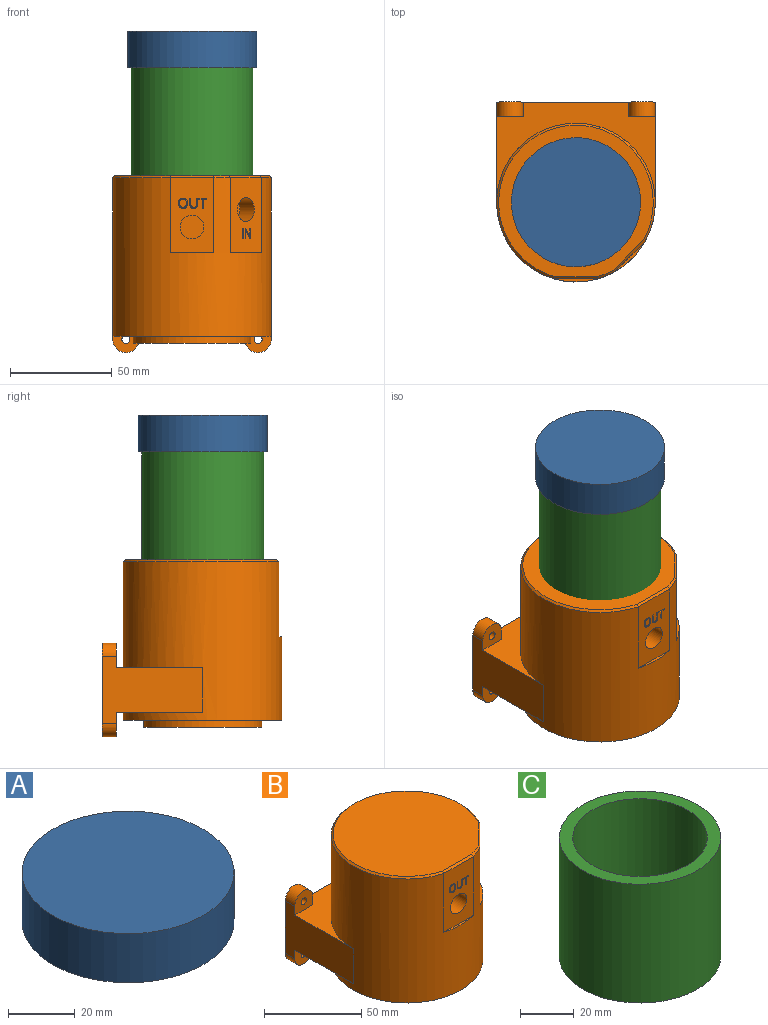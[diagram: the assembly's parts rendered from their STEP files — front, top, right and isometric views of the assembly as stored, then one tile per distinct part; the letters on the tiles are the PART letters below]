
ASSEMBLY  parts=3 mates=2
PART A: 3 faces, bbox 63.5x63.5x18 mm
  f0: cylinder r=31.75mm len=63.5mm, axis (0,0,-1), area 3590.8mm2, adj f1,f2
  f1: plane 63.5x63.5mm, normal (0,0,1), area 3166.9mm2, adj f0
  f2: plane 63.5x63.5mm, normal (0,0,-1), area 3166.9mm2, adj f0
PART B: 101 faces, bbox 78x88.5x87 mm
  f0: plane 37x15.15mm, normal (0.71,-0.71,0), area 674.2mm2, adj f5,f29,f32,f76,f77,f78,f79,f81
  f1: plane 37x21.42mm, normal (0,-1,0), area 655.2mm2, adj f5,f28,f30,f34,f35,f36,f37,f38
  f2: plane 76x74.5mm, normal (0,0,1), area 4494mm2, adj f97,f98,f99,f100
  f3: plane 78x49.5mm, normal (0,0,1), area 1289.8mm2, adj f5,f6,f7,f8,f9,f12,f19,f20
  f4: plane 78x49.5mm, normal (0,0,-1), area 1289.8mm2, adj f5,f6,f7,f8,f15,f16,f21,f24
  f5: cylinder r=39mm len=78mm, axis (0,0,-1), area 14811.9mm2, adj f0,f1,f3,f4,f6,f8,f25,f28
  f6: plane 49.5x33mm, normal (-1,0,0), area 1166mm2, adj f3,f4,f5,f7,f17,f20,f22,f24
  f7: plane 78x46mm, normal (0,1,0), area 2217.2mm2, adj f3,f4,f6,f8,f9,f10,f11,f13
  f8: plane 49.5x33mm, normal (1,0,0), area 1166mm2, adj f3,f4,f5,f7,f10,f12,f13,f16
  f9: plane 7x5.5mm, normal (-1,0,0), area 38.5mm2, adj f3,f7,f10,f12
  f10: cylinder r=6.5mm len=13mm, axis (0,1,0), area 142.9mm2, adj f7,f8,f9,f12
  f11: cylinder r=2mm len=7mm, axis (0,1,0), area 88mm2, adj f7,f12
  f12: plane 13x12mm, normal (0,-1,0), area 125.3mm2, adj f3,f8,f9,f10,f11
  f13: cylinder r=6.5mm len=13mm, axis (0,1,0), area 142.9mm2, adj f7,f8,f15,f16
  f14: cylinder r=2mm len=7mm, axis (0,1,0), area 88mm2, adj f7,f16
  f15: plane 7x5.5mm, normal (-1,0,0), area 38.5mm2, adj f4,f7,f13,f16
  f16: plane 13x12mm, normal (0,-1,0), area 125.3mm2, adj f4,f8,f13,f14,f15
  f17: cylinder r=6.5mm len=13mm, axis (0,1,0), area 142.9mm2, adj f6,f7,f19,f20
  f18: cylinder r=2mm len=7mm, axis (0,1,0), area 88mm2, adj f7,f20
  f19: plane 7x5.5mm, normal (1,0,0), area 38.5mm2, adj f3,f7,f17,f20
  f20: plane 13x12mm, normal (0,-1,0), area 125.3mm2, adj f3,f6,f17,f18,f19
  f21: plane 7x5.5mm, normal (1,0,0), area 38.5mm2, adj f4,f7,f22,f24
  f22: cylinder r=6.5mm len=13mm, axis (0,1,0), area 142.9mm2, adj f6,f7,f21,f24
  f23: cylinder r=2mm len=7mm, axis (0,1,0), area 88mm2, adj f7,f24
  f24: plane 13x12mm, normal (0,-1,0), area 125.3mm2, adj f4,f6,f21,f22,f23
  f25: plane 78x78mm, normal (0,0,-1), area 2136.3mm2, adj f5,f26
  f26: cylinder r=29mm len=58mm, axis (0,0,1), area 637.7mm2, adj f25,f27
  f27: plane 58x58mm, normal (0,0,-1), area 2642.1mm2, adj f26
  f28: plane 21.42x1.5mm, normal (0,0,1), area 21.5mm2, adj f1,f5
  f29: plane 15.15x15.15mm, normal (0,0,1), area 21.5mm2, adj f0,f5
  f30: cylinder r=5.85mm len=11.7mm, axis (0,-1,0), area 367.6mm2, adj f1,f31
  f31: plane 11.7x11.7mm, normal (0,-1,0), area 107.5mm2, adj f30
  f32: cylinder r=5.85mm len=15.34mm, axis (0.71,-0.71,0), area 367.6mm2, adj f0,f33
  f33: plane 11.7x8.27mm, normal (0.71,-0.71,0), area 107.5mm2, adj f32
  f34: plane 3.21x0.5mm, normal (-1,0,0), area 1.6mm2, adj f1,f35,f47,f48
  f35: plane 0.58x0.5mm, normal (0,0,-1), area 0.3mm2, adj f1,f34,f36,f48
  f36: plane 3.23x0.5mm, normal (1,0,0), area 1.6mm2, adj f1,f35,f37,f48
  f37: extruded ~0.96x0.5mm, area 0.5mm2, adj f1,f36,f38,f48
  f38: extruded ~0.97x0.5mm, area 0.5mm2, adj f1,f37,f39,f48
  f39: extruded ~1x0.5mm, area 0.5mm2, adj f1,f38,f40,f48
  f40: extruded ~0.95x0.5mm, area 0.5mm2, adj f1,f39,f41,f48
  f41: plane 3.23x0.5mm, normal (-1,0,0), area 1.6mm2, adj f1,f40,f42,f48
  f42: plane 0.58x0.5mm, normal (0,0,-1), area 0.3mm2, adj f1,f41,f43,f48
  f43: plane 3.19x0.5mm, normal (1,0,0), area 1.6mm2, adj f1,f42,f44,f48
  f44: extruded ~1.34x0.5mm, area 0.7mm2, adj f1,f43,f45,f48
  f45: extruded ~1.39x0.5mm, area 0.8mm2, adj f1,f44,f46,f48
  f46: extruded ~1.41x0.5mm, area 0.8mm2, adj f1,f45,f47,f48
  f47: extruded ~1.33x0.51mm, area 0.7mm2, adj f1,f34,f46,f48
  f48: plane 5.03x3.79mm, normal (0,-1,0), area 6.5mm2, adj f34,f35,f36,f37,f38,f39,f40,f41
  f49: extruded ~1.53x0.5mm, area 0.8mm2, adj f50,f64,f65,f75
  f50: extruded ~1.51x0.5mm, area 0.8mm2, adj f49,f51,f65,f75
  f51: extruded ~1.25x0.52mm, area 0.7mm2, adj f50,f52,f65,f75
  f52: extruded ~1.24x0.52mm, area 0.7mm2, adj f51,f53,f65,f75
  f53: extruded ~1.52x0.5mm, area 0.8mm2, adj f52,f54,f65,f75
  f54: extruded ~1.53x0.5mm, area 0.8mm2, adj f53,f55,f65,f75
  f55: extruded ~1.24x0.52mm, area 0.7mm2, adj f54,f64,f65,f75
  f56: extruded ~1.87x0.6mm, area 1mm2, adj f1,f57,f63,f65
  f57: extruded ~1.87x0.6mm, area 1mm2, adj f1,f56,f58,f65
  f58: extruded ~1.67x0.68mm, area 0.9mm2, adj f1,f57,f59,f65
  f59: extruded ~1.7x0.67mm, area 0.9mm2, adj f1,f58,f60,f65
  f60: extruded ~1.88x0.6mm, area 1mm2, adj f1,f59,f61,f65
  f61: extruded ~1.89x0.6mm, area 1mm2, adj f1,f60,f62,f65
  f62: extruded ~1.69x0.67mm, area 0.9mm2, adj f1,f61,f63,f65
  f63: extruded ~1.67x0.68mm, area 0.9mm2, adj f1,f56,f62,f65
  f64: extruded ~1.25x0.52mm, area 0.7mm2, adj f49,f55,f65,f75
  f65: plane 5.1x4.56mm, normal (0,-1,0), area 7.8mm2, adj f49,f50,f51,f52,f53,f54,f55,f56
  f66: plane 0.58x0.5mm, normal (0,0,1), area 0.3mm2, adj f1,f67,f73,f74
  f67: plane 4.45x0.5mm, normal (-1,0,0), area 2.2mm2, adj f1,f66,f68,f74
  f68: plane 1.57x0.5mm, normal (0,0,1), area 0.8mm2, adj f1,f67,f69,f74
  f69: plane 0.51x0.5mm, normal (-1,0,0), area 0.3mm2, adj f1,f68,f70,f74
  f70: plane 3.72x0.5mm, normal (0,0,-1), area 1.9mm2, adj f1,f69,f71,f74
  f71: plane 0.51x0.5mm, normal (1,0,0), area 0.3mm2, adj f1,f70,f72,f74
  f72: plane 1.57x0.5mm, normal (0,0,1), area 0.8mm2, adj f1,f71,f73,f74
  f73: plane 4.45x0.5mm, normal (1,0,0), area 2.2mm2, adj f1,f66,f72,f74
  f74: plane 4.96x3.72mm, normal (0,-1,0), area 4.5mm2, adj f66,f67,f68,f69,f70,f71,f72,f73
  f75: plane 4.08x3.34mm, normal (0,-1,0), area 11.3mm2, adj f49,f50,f51,f52,f53,f54,f55,f64
  f76: plane 4.96x0.35mm, normal (0.71,0.71,0), area 2.5mm2, adj f0,f77,f79,f80
  f77: plane 0.76x0.76mm, normal (0,0,1), area 0.3mm2, adj f0,f76,f78,f80
  f78: plane 4.96x0.35mm, normal (-0.71,-0.71,0), area 2.5mm2, adj f0,f77,f79,f80
  f79: plane 0.76x0.76mm, normal (0,0,-1), area 0.3mm2, adj f0,f76,f78,f80
  f80: plane 4.96x0.41mm, normal (0.71,-0.71,0), area 2.9mm2, adj f76,f77,f78,f79
  f81: plane 0.82x0.82mm, normal (0,0,1), area 0.3mm2, adj f0,f82,f95,f96
  f82: plane 4.96x0.35mm, normal (-0.71,-0.71,0), area 2.5mm2, adj f0,f81,f83,f96
  f83: plane 0.74x0.74mm, normal (0,0,-1), area 0.3mm2, adj f0,f82,f84,f96
  f84: plane 2.85x0.35mm, normal (0.71,0.71,0), area 1.4mm2, adj f0,f83,f85,f96
  f85: extruded ~0.71x0.37mm, area 0.4mm2, adj f0,f84,f86,f96
  f86: extruded ~0.59x0.38mm, area 0.3mm2, adj f0,f85,f87,f96
  f87: plane 0.37x0.37mm, normal (0,0,-1), area 0mm2, adj f0,f86,f88,f96
  f88: plane 4.14x2.26mm, normal (-0.59,-0.59,-0.55), area 2.5mm2, adj f0,f87,f89,f96
  f89: plane 0.81x0.81mm, normal (0,0,-1), area 0.3mm2, adj f0,f88,f90,f96
  f90: plane 4.96x0.35mm, normal (0.71,0.71,0), area 2.5mm2, adj f0,f89,f91,f96
  f91: plane 0.73x0.73mm, normal (0,0,1), area 0.3mm2, adj f0,f90,f92,f96
  f92: plane 2.82x0.35mm, normal (-0.71,-0.71,0), area 1.4mm2, adj f0,f91,f93,f96
  f93: extruded ~1.34x0.39mm, area 0.7mm2, adj f0,f92,f94,f96
  f94: plane 0.37x0.37mm, normal (0,0,1), area 0mm2, adj f0,f93,f95,f96
  f95: plane 4.16x2.27mm, normal (0.59,0.59,0.55), area 2.5mm2, adj f0,f81,f94,f96
  f96: plane 4.96x2.74mm, normal (0.71,-0.71,0), area 8.1mm2, adj f81,f82,f83,f84,f85,f86,f87,f88
  f97: plane 21.43x1mm, normal (0,-0.71,0.71), area 30.1mm2, adj f1,f2,f98,f99
  f98: cone r=38mm half-angle=45deg, axis (0,0,-1), area 12.3mm2, adj f2,f5,f97,f100
  f99: cone r=38mm half-angle=45deg, axis (0,0,-1), area 268.8mm2, adj f2,f5,f97,f100
  f100: plane 15.76x15.76mm, normal (0.5,-0.5,0.71), area 30.1mm2, adj f0,f2,f98,f99
PART C: 4 faces, bbox 60x60x54 mm
  f0: cylinder r=25mm len=54mm, axis (0,0,-1), area 8482.3mm2, adj f2,f3
  f1: cylinder r=30mm len=60mm, axis (0,0,-1), area 10178.8mm2, adj f2,f3
  f2: plane 60x60mm, normal (0,0,1), area 863.9mm2, adj f0,f1
  f3: plane 60x60mm, normal (0,0,-1), area 863.9mm2, adj f0,f1
PLACE A t=(0,0,6.5)mm
PLACE B t=(0,0,7.5)mm
PLACE C t=(0,0,6.5)mm
MATE fastened C.f0 <-> B.f5  axis (0,0,-1) through (0,0,81.5)mm
MATE fastened A.f0 <-> C.f0  axis (0,0,-1) through (0,0,135.5)mm
